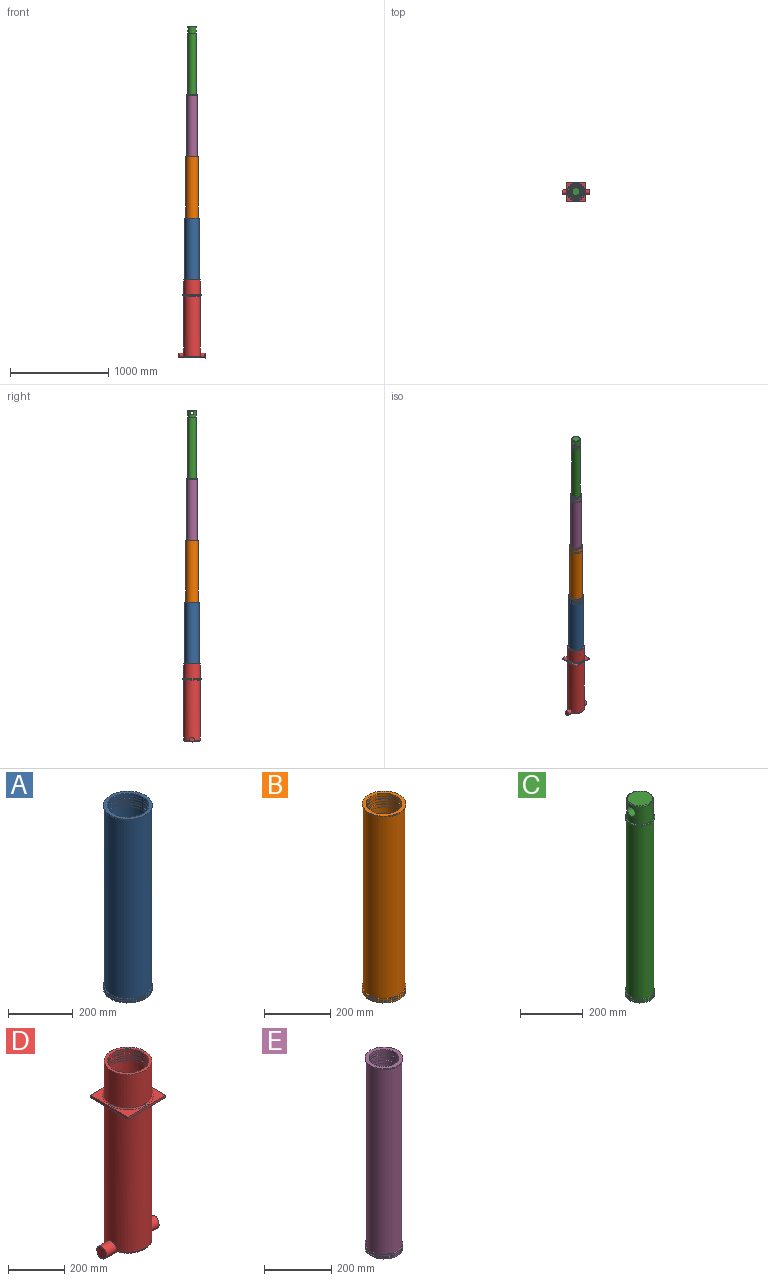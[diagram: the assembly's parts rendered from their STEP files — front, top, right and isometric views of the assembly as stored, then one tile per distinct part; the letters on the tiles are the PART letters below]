
ASSEMBLY  parts=5 mates=4
PART A: 21 faces, bbox 165.7x165.7x692.5 mm
  f0: cylinder r=63mm len=126mm, axis (0,0,-1), area 3562.6mm2, adj f1,f20
  f1: plane 130x130mm, normal (0,0,-1), area 804.2mm2, adj f0,f2
  f2: cylinder r=65mm len=130mm, axis (0,0,-1), area 4084.1mm2, adj f1,f3
  f3: plane 130x130mm, normal (0,0,1), area 804.2mm2, adj f2,f4
  f4: cylinder r=63mm len=126mm, axis (0,0,-1), area 3958.4mm2, adj f3,f5
  f5: plane 130x130mm, normal (0,0,-1), area 804.2mm2, adj f4,f6
  f6: cylinder r=65mm len=130mm, axis (0,0,-1), area 4084.1mm2, adj f5,f7
  f7: plane 130x130mm, normal (0,0,1), area 804.2mm2, adj f6,f8
  f8: cylinder r=63mm len=126mm, axis (0,0,-1), area 3958.4mm2, adj f7,f9
  f9: plane 132x132mm, normal (0,0,-1), area 1215.8mm2, adj f8,f10
  f10: cylinder r=66mm len=642.5mm, axis (0,0,-1), area 266438.5mm2, adj f9,f11
  f11: plane 151x151mm, normal (0,0,-1), area 4223.1mm2, adj f10,f12
  f12: cylinder r=75.5mm len=151mm, axis (0,0,-1), area 2846.3mm2, adj f11,f13
  f13: torus R=75.5mm, axis (0,0,-1), area 2207.2mm2, adj f12,f14
  f14: cylinder r=75.5mm len=151mm, axis (0,0,-1), area 2846.3mm2, adj f13,f15
  f15: plane 151x151mm, normal (0,0,1), area 1394.9mm2, adj f14,f16
  f16: cylinder r=72.5mm len=674.5mm, axis (0,0,-1), area 307255.6mm2, adj f15,f17
  f17: plane 151x151mm, normal (0,0,-1), area 1394.9mm2, adj f16,f18
  f18: cylinder r=75.5mm len=151mm, axis (0,0,-1), area 1423.1mm2, adj f17,f19
  f19: plane 151x151mm, normal (0,0,1), area 5039.9mm2, adj f18,f20
  f20: cone r=64mm half-angle=45deg, axis (0,0,1), area 564.2mm2, adj f0,f19
PART B: 21 faces, bbox 145.2x145.2x692.5 mm
  f0: cylinder r=53.5mm len=107mm, axis (0,0,-1), area 3361.5mm2, adj f1,f19
  f1: plane 111x111mm, normal (0,0,-1), area 684.9mm2, adj f0,f2
  f2: cylinder r=55.5mm len=111mm, axis (0,0,-1), area 3487.2mm2, adj f1,f3
  f3: plane 111x111mm, normal (0,0,1), area 684.9mm2, adj f2,f4
  f4: cylinder r=53.5mm len=107mm, axis (0,0,-1), area 3361.5mm2, adj f3,f5
  f5: plane 113x113mm, normal (0,0,-1), area 1036.7mm2, adj f4,f6
  f6: cylinder r=56.5mm len=642.5mm, axis (0,0,-1), area 228087.5mm2, adj f5,f7
  f7: plane 132x132mm, normal (0,0,-1), area 3656mm2, adj f6,f8
  f8: cylinder r=66mm len=132mm, axis (0,0,-1), area 2488.1mm2, adj f7,f9
  f9: torus R=66mm, axis (0,0,-1), area 1925.9mm2, adj f8,f10
  f10: cylinder r=66mm len=132mm, axis (0,0,-1), area 2488.1mm2, adj f9,f11
  f11: plane 132x132mm, normal (0,0,1), area 1215.8mm2, adj f10,f12
  f12: cylinder r=63mm len=674.5mm, axis (0,0,-1), area 266994.5mm2, adj f11,f13
  f13: plane 132x132mm, normal (0,0,-1), area 1215.8mm2, adj f12,f14
  f14: cylinder r=66mm len=132mm, axis (0,0,-1), area 1244.1mm2, adj f13,f15
  f15: plane 132x132mm, normal (0,0,1), area 4353.5mm2, adj f14,f20
  f16: cylinder r=53.5mm len=107mm, axis (0,0,-1), area 3025.4mm2, adj f17,f20
  f17: plane 111x111mm, normal (0,0,-1), area 684.9mm2, adj f16,f18
  f18: cylinder r=55.5mm len=111mm, axis (0,0,-1), area 3487.2mm2, adj f17,f19
  f19: plane 111x111mm, normal (0,0,1), area 684.9mm2, adj f0,f18
  f20: cone r=54.5mm half-angle=45deg, axis (0,0,1), area 479.8mm2, adj f15,f16
PART C: 25 faces, bbox 104.1x104.1x764.5 mm
  f0: plane 94x94mm, normal (0,0,1), area 1131mm2, adj f1,f23
  f1: cylinder r=43mm len=86mm, axis (0,0,-1), area 16561.6mm2, adj f0,f2,f24
  f2: torus R=40mm, axis (0,0,-1), area 1240.9mm2, adj f1,f3
  f3: plane 80x80mm, normal (0,0,1), area 5026.5mm2, adj f2
  f4: plane 69x69mm, normal (0,0,-1), area 3739.3mm2, adj f5
  f5: cylinder r=34.5mm len=69mm, axis (0,0,-1), area 1517.4mm2, adj f4,f6
  f6: plane 73x73mm, normal (0,0,-1), area 446.1mm2, adj f5,f7
  f7: cylinder r=36.5mm len=73mm, axis (0,0,-1), area 2293.4mm2, adj f6,f8
  f8: plane 73x73mm, normal (0,0,1), area 446.1mm2, adj f7,f9
  f9: cylinder r=34.5mm len=69mm, axis (0,0,-1), area 2167.7mm2, adj f8,f10
  f10: plane 73x73mm, normal (0,0,-1), area 446.1mm2, adj f9,f11
  f11: cylinder r=36.5mm len=73mm, axis (0,0,-1), area 2293.4mm2, adj f10,f12
  f12: plane 73x73mm, normal (0,0,1), area 446.1mm2, adj f11,f13
  f13: cylinder r=34.5mm len=69mm, axis (0,0,-1), area 2167.7mm2, adj f12,f14
  f14: plane 75x75mm, normal (0,0,-1), area 678.6mm2, adj f13,f15
  f15: cylinder r=37.5mm len=642.5mm, axis (0,0,-1), area 151385.5mm2, adj f14,f16
  f16: plane 94x94mm, normal (0,0,-1), area 2521.9mm2, adj f15,f17
  f17: cylinder r=47mm len=94mm, axis (0,0,-1), area 1771.9mm2, adj f16,f18
  f18: torus R=47mm, axis (0,0,-1), area 1363.3mm2, adj f17,f19
  f19: cylinder r=47mm len=94mm, axis (0,0,-1), area 1771.9mm2, adj f18,f20
  f20: plane 94x94mm, normal (0,0,1), area 857.7mm2, adj f19,f21
  f21: cylinder r=44mm len=674.5mm, axis (0,0,-1), area 186472.4mm2, adj f20,f22
  f22: plane 94x94mm, normal (0,0,-1), area 857.7mm2, adj f21,f23
  f23: cylinder r=47mm len=94mm, axis (0,0,-1), area 885.9mm2, adj f0,f22
  f24: cylinder r=18mm len=86mm, axis (1,0,0), area 9284.5mm2, adj f1
PART D: 42 faces, bbox 270x202.5x793 mm
  f0: cylinder r=85mm len=773mm, axis (0,0,-1), area 399705.8mm2, adj f12,f19,f21,f22,f25,f26,f30,f34
  f1: cylinder r=76.5mm len=703mm, axis (0,0,-1), area 337343.3mm2, adj f2,f3,f11,f20
  f2: plane 147.68x56.5mm, normal (0,0,1), area 6167.9mm2, adj f1,f20
  f3: plane 147.68x56.5mm, normal (0,0,1), area 6167.9mm2, adj f1,f20
  f4: plane 144.57x55mm, normal (0,0,-1), area 5871.7mm2, adj f19,f22
  f5: plane 144.57x55mm, normal (0,0,-1), area 5871.7mm2, adj f19,f21
  f6: cylinder r=72.5mm len=145mm, axis (0,0,-1), area 4555.3mm2, adj f7,f16
  f7: plane 149x149mm, normal (0,0,-1), area 923.6mm2, adj f6,f8
  f8: cylinder r=74.5mm len=149mm, axis (0,0,-1), area 4681mm2, adj f7,f9
  f9: plane 149x149mm, normal (0,0,1), area 923.6mm2, adj f8,f10
  f10: cylinder r=72.5mm len=145mm, axis (0,0,-1), area 4555.3mm2, adj f9,f11
  f11: plane 153x153mm, normal (0,0,-1), area 1872.4mm2, adj f1,f10
  f12: plane 170x170mm, normal (0,0,1), area 5726.3mm2, adj f0,f23
  f13: cylinder r=72.5mm len=145mm, axis (0,0,-1), area 4099.8mm2, adj f14,f23
  f14: plane 149x149mm, normal (0,0,-1), area 923.6mm2, adj f13,f15
  f15: cylinder r=74.5mm len=149mm, axis (0,0,-1), area 4681mm2, adj f14,f16
  f16: plane 149x149mm, normal (0,0,1), area 923.6mm2, adj f6,f15
  f17: cylinder r=85mm len=50mm, axis (0,0,-1), area 1985.2mm2, adj f19
  f18: cylinder r=85mm len=50mm, axis (0,0,-1), area 1985.2mm2, adj f19
  f19: cylinder r=25mm len=270mm, axis (-1,0,0), area 23610.7mm2, adj f0,f4,f5,f17,f18,f21,f22
  f20: cylinder r=25mm len=153mm, axis (-1,0,0), area 7001.4mm2, adj f1,f2,f3
  f21: torus R=75mm, axis (0,0,1), area 3315.3mm2, adj f0,f5,f19
  f22: torus R=75mm, axis (0,0,1), area 3315.3mm2, adj f0,f4,f19
  f23: cone r=73.5mm half-angle=45deg, axis (0,0,1), area 648.7mm2, adj f12,f13
  f24: plane 94.5x10mm, normal (0,1,0), area 945mm2, adj f25,f28,f29,f37
  f25: plane 20.02x10.02mm, normal (-1,0,0), area 110.7mm2, adj f0,f24,f29,f37,f39,f41
  f26: plane 20.02x10.02mm, normal (-1,0,0), area 110.7mm2, adj f0,f27,f29,f37,f39,f41
  f27: plane 94.5x10mm, normal (0,-1,0), area 945mm2, adj f26,f28,f29,f37
  f28: plane 190x10mm, normal (1,0,0), area 1900mm2, adj f24,f27,f29,f37
  f29: plane 190x94.5mm, normal (0,0,-1), area 5321.5mm2, adj f24,f25,f26,f27,f28,f41
  f30: plane 20.02x10.02mm, normal (1,0,0), area 110.7mm2, adj f0,f31,f35,f36,f38,f40
  f31: plane 94.5x10mm, normal (0,1,0), area 945mm2, adj f30,f32,f35,f36
  f32: plane 190x10mm, normal (-1,0,0), area 1900mm2, adj f31,f33,f35,f36
  f33: plane 94.5x10mm, normal (0,-1,0), area 945mm2, adj f32,f34,f35,f36
  f34: plane 20.02x10.02mm, normal (1,0,0), area 110.7mm2, adj f0,f33,f35,f36,f38,f40
  f35: plane 190x94.5mm, normal (0,0,-1), area 5321.5mm2, adj f30,f31,f32,f33,f34,f40
  f36: plane 190x94.5mm, normal (0,0,1), area 5321.5mm2, adj f30,f31,f32,f33,f34,f38
  f37: plane 190x94.5mm, normal (0,0,1), area 5321.5mm2, adj f24,f25,f26,f27,f28,f39
  f38: torus R=90mm, axis (0,0,1), area 2134.3mm2, adj f0,f30,f34,f36
  f39: torus R=90mm, axis (0,0,1), area 2134.3mm2, adj f0,f25,f26,f37
  f40: torus R=90mm, axis (0,0,1), area 2134.3mm2, adj f0,f30,f34,f35
  f41: torus R=90mm, axis (0,0,1), area 2134.3mm2, adj f0,f25,f26,f29
PART E: 20 faces, bbox 124.6x124.6x692.5 mm
  f0: plane 113x113mm, normal (0,0,1), area 1036.7mm2, adj f1,f19
  f1: cylinder r=53.5mm len=674.5mm, axis (0,0,-1), area 226733.5mm2, adj f0,f2
  f2: plane 113x113mm, normal (0,0,-1), area 1036.7mm2, adj f1,f3
  f3: cylinder r=56.5mm len=113mm, axis (0,0,-1), area 1065mm2, adj f2,f4
  f4: plane 113x113mm, normal (0,0,1), area 3946.6mm2, adj f3,f5
  f5: cylinder r=44mm len=88mm, axis (0,0,-1), area 2764.6mm2, adj f4,f6
  f6: plane 92x92mm, normal (0,0,-1), area 565.5mm2, adj f5,f7
  f7: cylinder r=46mm len=92mm, axis (0,0,-1), area 2890.3mm2, adj f6,f8
  f8: plane 92x92mm, normal (0,0,1), area 565.5mm2, adj f7,f9
  f9: cylinder r=44mm len=88mm, axis (0,0,-1), area 2764.6mm2, adj f8,f10
  f10: plane 92x92mm, normal (0,0,-1), area 565.5mm2, adj f9,f11
  f11: cylinder r=46mm len=92mm, axis (0,0,-1), area 2890.3mm2, adj f10,f12
  f12: plane 92x92mm, normal (0,0,1), area 565.5mm2, adj f11,f13
  f13: cylinder r=44mm len=88mm, axis (0,0,-1), area 2764.6mm2, adj f12,f14
  f14: plane 94x94mm, normal (0,0,-1), area 857.7mm2, adj f13,f15
  f15: cylinder r=47mm len=642.5mm, axis (0,0,-1), area 189736.5mm2, adj f14,f16
  f16: plane 113x113mm, normal (0,0,-1), area 3089mm2, adj f15,f17
  f17: cylinder r=56.5mm len=113mm, axis (0,0,-1), area 2130mm2, adj f16,f18
  f18: torus R=56.5mm, axis (0,0,-1), area 1644.6mm2, adj f17,f19
  f19: cylinder r=56.5mm len=113mm, axis (0,0,-1), area 2130mm2, adj f0,f18
PLACE A t=(-375.89,-86.8,505.29)mm
PLACE B t=(-375.89,-86.8,1133.79)mm
PLACE C t=(-375.89,-86.8,2402.79)mm
PLACE D rot(axis=(0.86,0.27,-0.43),0deg) t=(-375.89,-86.8,-182.71)mm fixed
PLACE E t=(-375.89,-86.8,1775.79)mm
MATE slider B.f0 <-> A.f0  axis (0,0,-1) through (-375.89,-86.8,1823.29)mm
MATE slider A.f0 <-> D.f0  axis (0,0,-1) through (-375.89,-86.8,520.29)mm
MATE slider C.f1 <-> E.f1  axis (0,0,-1) through (-375.89,-86.8,3077.29)mm
MATE slider E.f1 <-> B.f0  axis (0,0,-1) through (-375.89,-86.8,2450.29)mm
